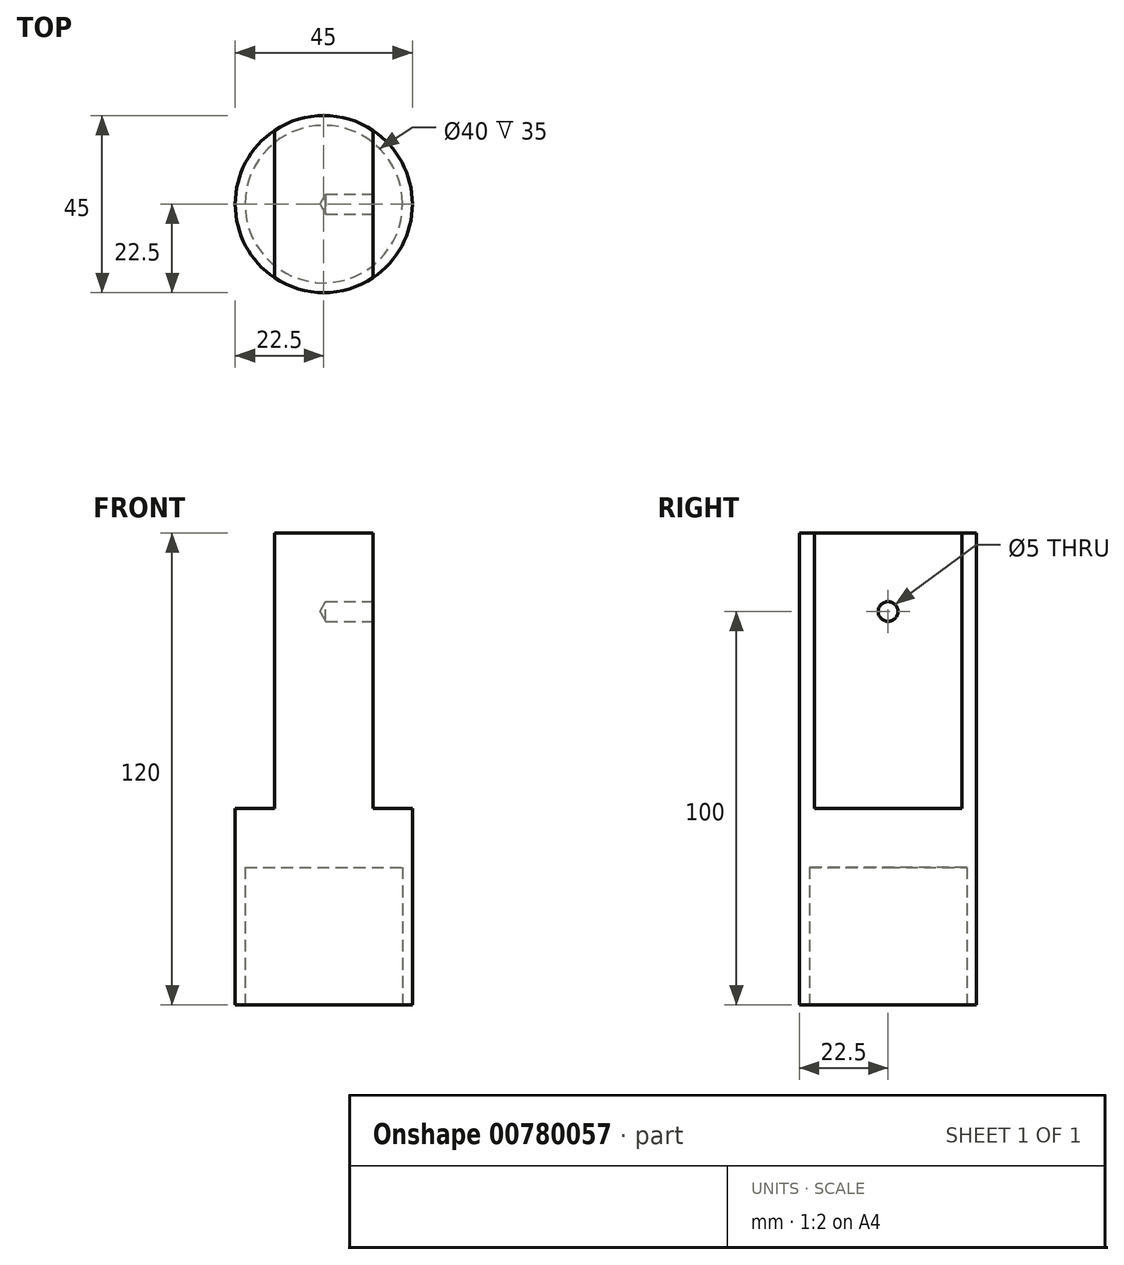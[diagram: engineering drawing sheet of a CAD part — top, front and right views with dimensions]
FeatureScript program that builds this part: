
annotation { "Feature Type Name" : "Feature", "Feature Type Description" : "" }
export const myFeature = defineFeature(function(context is Context, id is Id, definition is map)
    precondition{}
    {
        {
            var Q0;
            Q0=qCreatedBy(makeId("Top.planeOp"),FACE);
            var sketch = newSketch(context, id + "F0", { "sketchPlane" : qUnion([Q0])});
            skCircle(sketch, "E0", {"center": v(0, 0) * mm, "radius": 22.5 * mm});
            skSolve(sketch);
        }
        {
            var Q0;
            Q0=makeQuery(id+"F0.imprint","IMPRINT",FACE,{"disambiguationData":[TD([[makeQuery(id+"F0.imprint","IMPRINT",EDGE,{"derivedFrom":sQuery(id+"F0.wireOp",EDGE,"E0")}),1.0]])]});
            extrude(context, id + "F1", {"entities" : qUnion([Q0]), "depth" : 120 * mm, "offsetDistance" : 25 * mm});
        }
        {
            var Q0;
            Q0=makeQuery(id+"F1.opExtrude","CAP_FACE",FACE,{"disambiguationData":[OSD([sQuery(id+"F0.wireOp",EDGE,"E0")])],"isStart":false});
            var sketch = newSketch(context, id + "F2", { "sketchPlane" : qUnion([Q0])});
            skLineSegment(sketch, "E1", {"start": v(-12.5, 18.7) * mm, "end": v(-12.5, -18.7) * mm});
            skLineSegment(sketch, "E2", {"start": v(12.5, -18.7) * mm, "end": v(12.5, 18.7) * mm});
            skSolve(sketch);
        }
        {
            var Q0;
            {var subQ0=sQuery(id+"F2.wireOp",EDGE,"E2");Q0=makeQuery(id+"F2.imprint","IMPRINT",FACE,{"disambiguationData":[TD([[makeQuery(id+"F2.imprint","IMPRINT",EDGE,{"derivedFrom":subQ0}),-1.0]])]});}
            var Q1;
            {var subQ0=sQuery(id+"F2.wireOp",EDGE,"E1");Q1=makeQuery(id+"F2.imprint","IMPRINT",FACE,{"disambiguationData":[TD([[makeQuery(id+"F2.imprint","IMPRINT",EDGE,{"derivedFrom":subQ0}),-1.0]])]});}
            extrude(context, id + "F3", {"entities" : qUnion([Q0, Q1]), "operationType" : NewBodyOperationType.REMOVE, "oppositeDirection" : true, "depth" : 70 * mm, "offsetDistance" : 25 * mm});
        }
        {
            var Q0;
            Q0=makeQuery(id+"F1.opExtrude","CAP_FACE",FACE,{"disambiguationData":[OSD([sQuery(id+"F0.wireOp",EDGE,"E0")])],"isStart":true});
            var sketch = newSketch(context, id + "F4", { "sketchPlane" : qUnion([Q0])});
            skCircle(sketch, "E3", {"center": v(0, 0) * mm, "radius": 20 * mm});
            skSolve(sketch);
        }
        {
            var Q0;
            Q0=makeQuery(id+"F4.imprint","IMPRINT",FACE,{"disambiguationData":[TD([[makeQuery(id+"F4.imprint","IMPRINT",EDGE,{"derivedFrom":sQuery(id+"F4.wireOp",EDGE,"E3")}),1.0]])]});
            extrude(context, id + "F5", {"entities" : qUnion([Q0]), "operationType" : NewBodyOperationType.REMOVE, "oppositeDirection" : true, "depth" : 35 * mm, "offsetDistance" : 25 * mm});
        }
        {
            var Q0;
            Q0=makeQuery(id+"F3.boolean.opBoolean","COPY",FACE,{"derivedFrom":makeQuery(id+"F3.opExtrude","SWEPT_FACE",FACE,{"disambiguationData":[OSD([sQuery(id+"F2.wireOp",EDGE,"E2")])]})});
            var sketch = newSketch(context, id + "F6", { "sketchPlane" : qUnion([Q0])});
            skPoint(sketch, "E4", {"position": v(0, 100) * mm});
            skSolve(sketch);
        }
        {
            var Q0;
            Q0=sQuery(id+"F6.wireOp",VERTEX,"E4");
            var Q1;
            Q1=makeQuery(id+"F1.opExtrude","SWEPT_BODY",BODY,{"disambiguationData":[OSD([sQuery(id+"F0.wireOp",EDGE,"E0")])]});
            hole(context, id + "F7", {"style" : HoleStyle.SIMPLE, "endStyle" : HoleEndStyle.BLIND, "holeDiameter" : 5 * mm, "majorDiameter" : 5 * mm, "holeDepth" : 12 * mm, "isTappedThrough" : true, "tappedDepth" : 12 * mm, "tapClearance" : 3, "locations" : qUnion([Q0]), "scope" : qUnion([Q1])});
        }
    });
